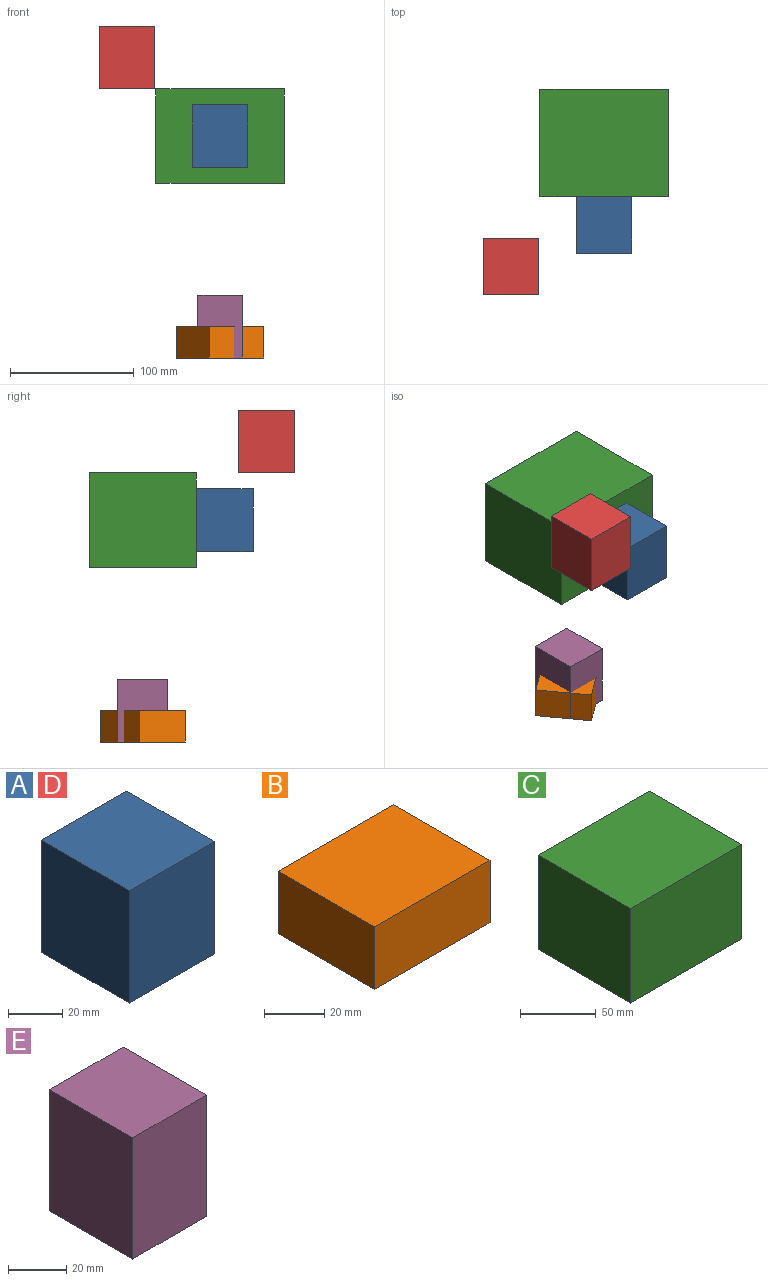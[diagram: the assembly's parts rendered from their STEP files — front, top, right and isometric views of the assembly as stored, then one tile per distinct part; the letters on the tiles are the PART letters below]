
ASSEMBLY  parts=5 mates=4
PART A: 6 faces, bbox 44.5x45.8x50.8 mm
  f0: plane 50.8x44.5mm, normal (0,1,0), area 2260.4mm2, adj f1,f3,f4,f5
  f1: plane 50.8x45.82mm, normal (-1,0,0), area 2327.5mm2, adj f0,f2,f4,f5
  f2: plane 50.8x44.5mm, normal (0,-1,0), area 2260.4mm2, adj f1,f3,f4,f5
  f3: plane 50.8x45.82mm, normal (1,0,0), area 2327.5mm2, adj f0,f2,f4,f5
  f4: plane 45.82x44.5mm, normal (0,0,1), area 2038.7mm2, adj f0,f1,f2,f3
  f5: plane 45.82x44.5mm, normal (0,0,-1), area 2038.7mm2, adj f0,f1,f2,f3
PART B: 6 faces, bbox 54.3x45.4x25.4 mm
  f0: plane 45.37x25.4mm, normal (-1,0,0), area 1152.3mm2, adj f1,f3,f4,f5
  f1: plane 54.27x25.4mm, normal (0,-1,0), area 1378.5mm2, adj f0,f2,f4,f5
  f2: plane 45.37x25.4mm, normal (1,0,0), area 1152.3mm2, adj f1,f3,f4,f5
  f3: plane 54.27x25.4mm, normal (0,1,0), area 1378.5mm2, adj f0,f2,f4,f5
  f4: plane 54.27x45.37mm, normal (0,0,1), area 2462.1mm2, adj f0,f1,f2,f3
  f5: plane 54.27x45.37mm, normal (0,0,-1), area 2462.1mm2, adj f0,f1,f2,f3
PART C: 6 faces, bbox 103.6x86.6x76.2 mm
  f0: plane 103.57x76.2mm, normal (0,1,0), area 7892.3mm2, adj f1,f3,f4,f5
  f1: plane 86.59x76.2mm, normal (-1,0,0), area 6598mm2, adj f0,f2,f4,f5
  f2: plane 103.57x76.2mm, normal (0,-1,0), area 7892.3mm2, adj f1,f3,f4,f5
  f3: plane 86.59x76.2mm, normal (1,0,0), area 6598mm2, adj f0,f2,f4,f5
  f4: plane 103.57x86.59mm, normal (0,0,1), area 8968.2mm2, adj f0,f1,f2,f3
  f5: plane 103.57x86.59mm, normal (0,0,-1), area 8968.2mm2, adj f0,f1,f2,f3
PART D: same geometry as A
PART E: 6 faces, bbox 35.8x40.3x50.8 mm
  f0: plane 50.8x35.82mm, normal (0,1,0), area 1819.8mm2, adj f1,f3,f4,f5
  f1: plane 50.8x40.35mm, normal (-1,0,0), area 2049.7mm2, adj f0,f2,f4,f5
  f2: plane 50.8x35.82mm, normal (0,-1,0), area 1819.8mm2, adj f1,f3,f4,f5
  f3: plane 50.8x40.35mm, normal (1,0,0), area 2049.7mm2, adj f0,f2,f4,f5
  f4: plane 40.35x35.82mm, normal (0,0,1), area 1445.4mm2, adj f0,f1,f2,f3
  f5: plane 40.35x35.82mm, normal (0,0,-1), area 1445.4mm2, adj f0,f1,f2,f3
PLACE A t=(155.81,-246.86,107.54)mm
PLACE B rot(axis=(0,0,1),35.9deg) t=(111.65,-180.72,-46)mm
PLACE C t=(120.36,-146.44,94.84)mm fixed
PLACE D t=(80.85,-280.58,171.04)mm
PLACE E t=(78.31,-108.73,-46)mm
MATE fastened C.f2 <-> A.f0  axis (0,-1,0) through (120.36,-189.73,132.94)mm
MATE slider E.f4 <-> C.f5  axis (0,0,1) through (120.36,-146.44,4.8)mm
MATE revolute B.f5 <-> E.f5  axis (0,0,-1) through (120.36,-146.44,-46)mm
MATE planar C.f4 <-> D.f5  axis (0,0,1) through (120.36,-146.44,171.04)mm
